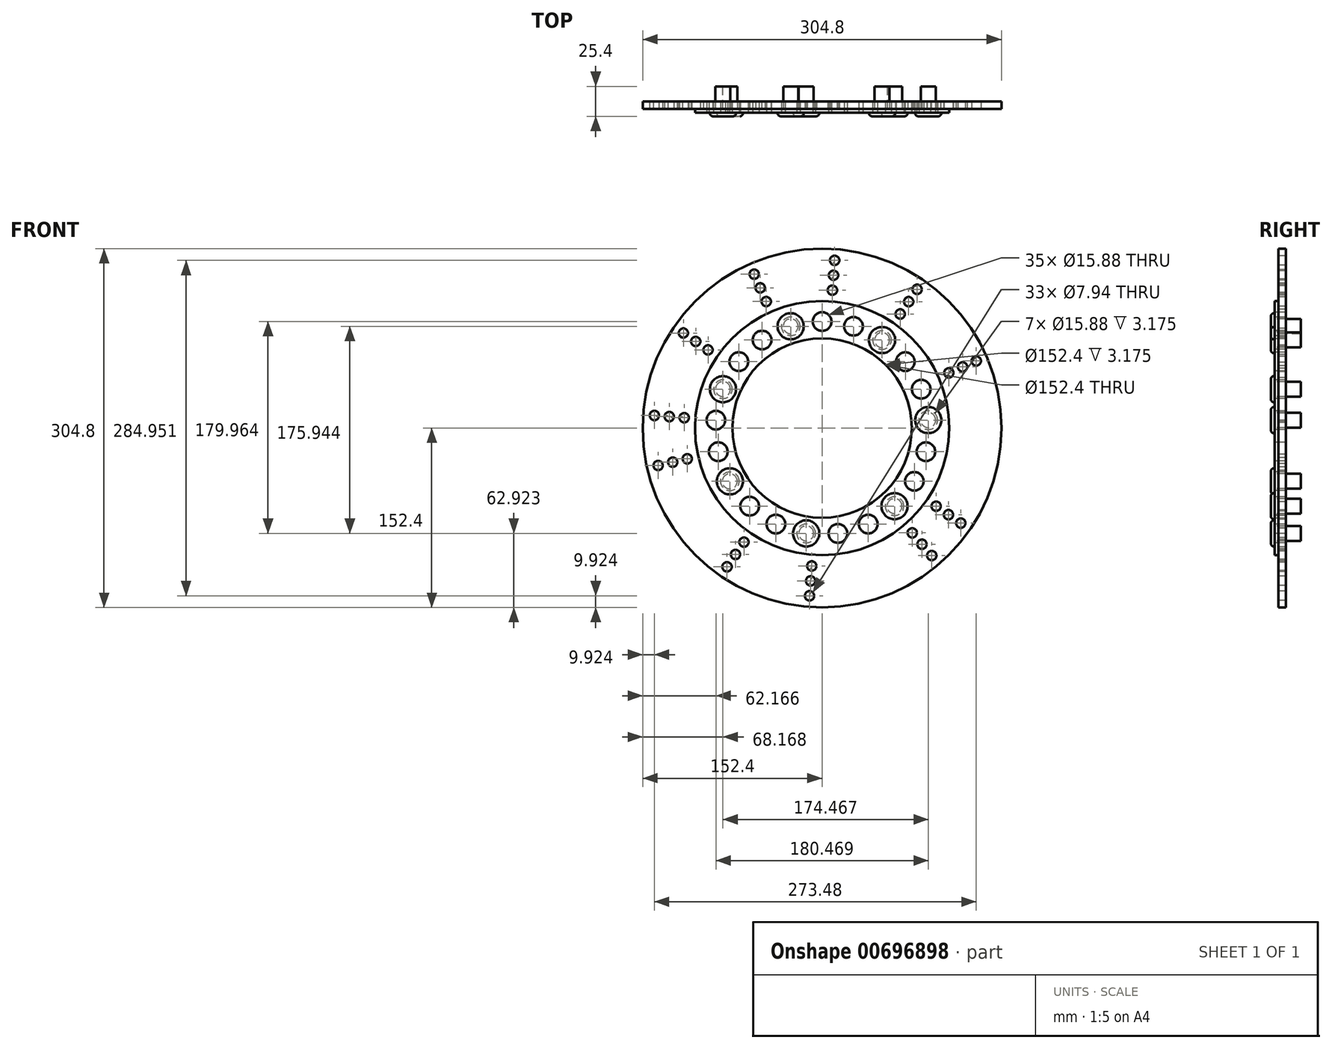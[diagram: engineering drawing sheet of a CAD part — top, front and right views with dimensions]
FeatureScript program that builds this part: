
annotation { "Feature Type Name" : "Feature", "Feature Type Description" : "" }
export const myFeature = defineFeature(function(context is Context, id is Id, definition is map)
    precondition{}
    {
        {
            var Q0;
            Q0=qCreatedBy(makeId("Front.planeOp"),FACE);
            var sketch = newSketch(context, id + "F0", { "sketchPlane" : qUnion([Q0])});
            skCircle(sketch, "E0", {"center": v(0, 0) * mm, "radius": 152.4 * mm});
            skCircle(sketch, "E1", {"center": v(0, 0) * mm, "radius": 76.2 * mm});
            skSolve(sketch);
        }
        {
            var Q0;
            Q0=qSketchRegion(id+"F0",true);
            extrude(context, id + "F1", {"entities" : qUnion([Q0]), "depth" : 6.35 * mm, "offsetDistance" : 25.4 * mm});
        }
        {
            var Q0;
            Q0=makeQuery(id+"F1.opExtrude","CAP_FACE",FACE,{"disambiguationData":[OSD([sQuery(id+"F0.wireOp",EDGE,"E0"),sQuery(id+"F0.wireOp",EDGE,"E1")])],"isStart":false});
            var sketch = newSketch(context, id + "F2", { "sketchPlane" : qUnion([Q0])});
            skCircle(sketch, "E2", {"center": v(0, 0) * mm, "radius": 76.2 * mm});
            skCircle(sketch, "E3", {"center": v(0, 0) * mm, "radius": 107.95 * mm});
            skSolve(sketch);
        }
        {
            var Q0;
            Q0=qSketchRegion(id+"F2",true);
            extrude(context, id + "F3", {"entities" : qUnion([Q0]), "depth" : 3.17 * mm, "offsetDistance" : 25.4 * mm});
        }
        {
            var Q0;
            Q0=makeQuery(id+"F3.opExtrude","CAP_FACE",FACE,{"disambiguationData":[OSD([sQuery(id+"F2.wireOp",EDGE,"E2"),sQuery(id+"F2.wireOp",EDGE,"E3")])],"isStart":false});
            var sketch = newSketch(context, id + "F4", { "sketchPlane" : qUnion([Q0])});
            skCircle(sketch, "E4", {"center": v(0, 90.49) * mm, "radius": 7.94 * mm});
            skCircle(sketch, "E5.1.0", {"center": v(-26.67, 86.47) * mm, "radius": 7.94 * mm});
            skCircle(sketch, "E5.2.0", {"center": v(-50.97, 74.76) * mm, "radius": 7.94 * mm});
            skCircle(sketch, "E5.3.0", {"center": v(-70.75, 56.42) * mm, "radius": 7.94 * mm});
            skCircle(sketch, "E5.4.0", {"center": v(-84.23, 33.06) * mm, "radius": 7.94 * mm});
            skCircle(sketch, "E5.5.0", {"center": v(-90.23, 6.76) * mm, "radius": 7.94 * mm});
            skCircle(sketch, "E5.6.0", {"center": v(-88.22, -20.14) * mm, "radius": 7.94 * mm});
            skCircle(sketch, "E5.7.0", {"center": v(-78.36, -45.24) * mm, "radius": 7.94 * mm});
            skCircle(sketch, "E5.8.0", {"center": v(-61.55, -66.33) * mm, "radius": 7.94 * mm});
            skCircle(sketch, "E5.9.0", {"center": v(-39.26, -81.53) * mm, "radius": 7.94 * mm});
            skCircle(sketch, "E5.10.0", {"center": v(-13.49, -89.48) * mm, "radius": 7.94 * mm});
            skCircle(sketch, "E5.11.0", {"center": v(13.49, -89.48) * mm, "radius": 7.94 * mm});
            skCircle(sketch, "E5.12.0", {"center": v(39.26, -81.53) * mm, "radius": 7.94 * mm});
            skCircle(sketch, "E5.13.0", {"center": v(61.55, -66.33) * mm, "radius": 7.94 * mm});
            skCircle(sketch, "E5.14.0", {"center": v(78.36, -45.24) * mm, "radius": 7.94 * mm});
            skCircle(sketch, "E5.15.0", {"center": v(88.22, -20.14) * mm, "radius": 7.94 * mm});
            skCircle(sketch, "E5.16.0", {"center": v(90.23, 6.76) * mm, "radius": 7.94 * mm});
            skCircle(sketch, "E5.17.0", {"center": v(84.23, 33.06) * mm, "radius": 7.94 * mm});
            skCircle(sketch, "E5.18.0", {"center": v(70.75, 56.42) * mm, "radius": 7.94 * mm});
            skCircle(sketch, "E5.19.0", {"center": v(50.97, 74.76) * mm, "radius": 7.94 * mm});
            skPoint(sketch, "E5.center", {"position": v(0, 0) * mm});
            skCircle(sketch, "E6.1.20.0", {"center": v(26.67, 86.47) * mm, "radius": 7.94 * mm});
            skSolve(sketch);
        }
        {
            var Q0;
            Q0=qSketchRegion(id+"F4",true);
            extrude(context, id + "F5", {"entities" : qUnion([Q0]), "operationType" : NewBodyOperationType.REMOVE, "endBound" : BoundingType.THROUGH_ALL, "oppositeDirection" : true, "depth" : 25.4 * mm, "offsetDistance" : 25.4 * mm});
        }
        {
            var Q0;
            Q0=makeQuery(id+"F3.opExtrude","CAP_FACE",FACE,{"disambiguationData":[OSD([sQuery(id+"F2.wireOp",EDGE,"E2"),sQuery(id+"F2.wireOp",EDGE,"E3")])],"isStart":false});
            var sketch = newSketch(context, id + "F6", { "sketchPlane" : qUnion([Q0])});
            skCircle(sketch, "E7", {"center": v(-13.49, -89.48) * mm, "radius": 11.11 * mm});
            skCircle(sketch, "E8", {"center": v(-78.36, -45.24) * mm, "radius": 11.11 * mm});
            skCircle(sketch, "E9", {"center": v(-84.23, 33.06) * mm, "radius": 11.11 * mm});
            skCircle(sketch, "E10", {"center": v(-26.67, 86.47) * mm, "radius": 11.11 * mm});
            skCircle(sketch, "E11", {"center": v(50.97, 74.76) * mm, "radius": 11.11 * mm});
            skCircle(sketch, "E12", {"center": v(90.23, 6.76) * mm, "radius": 11.11 * mm});
            skCircle(sketch, "E13", {"center": v(61.55, -66.33) * mm, "radius": 11.11 * mm});
            skSolve(sketch);
        }
        {
            var Q0;
            Q0=qSketchRegion(id+"F6",true);
            extrude(context, id + "F7", {"entities" : qUnion([Q0]), "operationType" : NewBodyOperationType.ADD, "depth" : 3.17 * mm, "offsetDistance" : 25.4 * mm});
        }
        {
            var Q0;
            Q0=makeQuery(id+"F1.opExtrude","CAP_FACE",FACE,{"disambiguationData":[OSD([sQuery(id+"F0.wireOp",EDGE,"E0"),sQuery(id+"F0.wireOp",EDGE,"E1")])],"isStart":false});
            var sketch = newSketch(context, id + "F8", { "sketchPlane" : qUnion([Q0])});
            skLineSegment(sketch, "E14", {"start": v(0, 107.95) * mm, "end": v(0, 152.4) * mm, "construction": true});
            skLineSegment(sketch, "E15", {"start": v(-7.94, 116.43) * mm, "end": v(7.94, 143.92) * mm, "construction": true});
            skCircle(sketch, "E16", {"center": v(0, 130.17) * mm, "radius": 3.97 * mm});
            skCircle(sketch, "E17", {"center": v(-7.94, 116.43) * mm, "radius": 3.97 * mm});
            skCircle(sketch, "E18", {"center": v(7.94, 143.92) * mm, "radius": 3.97 * mm});
            skCircle(sketch, "E19.1.0", {"center": v(-49.82, 120.27) * mm, "radius": 3.97 * mm});
            skCircle(sketch, "E19.1.1", {"center": v(-47.74, 136) * mm, "radius": 3.97 * mm});
            skCircle(sketch, "E19.1.2", {"center": v(-51.89, 104.53) * mm, "radius": 3.97 * mm});
            skCircle(sketch, "E19.2.0", {"center": v(-92.05, 92.05) * mm, "radius": 3.97 * mm});
            skCircle(sketch, "E19.2.1", {"center": v(-96.16, 107.38) * mm, "radius": 3.97 * mm});
            skCircle(sketch, "E19.2.2", {"center": v(-87.94, 76.71) * mm, "radius": 3.97 * mm});
            skCircle(sketch, "E19.3.0", {"center": v(-120.27, 49.82) * mm, "radius": 3.97 * mm});
            skCircle(sketch, "E19.3.1", {"center": v(-129.93, 62.41) * mm, "radius": 3.97 * mm});
            skCircle(sketch, "E19.3.2", {"center": v(-110.6, 37.22) * mm, "radius": 3.97 * mm});
            skCircle(sketch, "E19.4.0", {"center": v(-130.17, 0) * mm, "radius": 3.97 * mm});
            skCircle(sketch, "E19.4.1", {"center": v(-143.92, 7.94) * mm, "radius": 3.97 * mm});
            skCircle(sketch, "E19.4.2", {"center": v(-116.43, -7.94) * mm, "radius": 3.97 * mm});
            skCircle(sketch, "E19.5.0", {"center": v(-120.27, -49.82) * mm, "radius": 3.97 * mm});
            skCircle(sketch, "E19.5.1", {"center": v(-136, -47.74) * mm, "radius": 3.97 * mm});
            skCircle(sketch, "E19.5.2", {"center": v(-104.53, -51.89) * mm, "radius": 3.97 * mm});
            skCircle(sketch, "E19.6.0", {"center": v(-92.05, -92.05) * mm, "radius": 3.97 * mm});
            skCircle(sketch, "E19.6.1", {"center": v(-107.38, -96.16) * mm, "radius": 3.97 * mm});
            skCircle(sketch, "E19.6.2", {"center": v(-76.71, -87.94) * mm, "radius": 3.97 * mm});
            skCircle(sketch, "E19.7.0", {"center": v(-49.82, -120.27) * mm, "radius": 3.97 * mm});
            skCircle(sketch, "E19.7.1", {"center": v(-62.41, -129.93) * mm, "radius": 3.97 * mm});
            skCircle(sketch, "E19.7.2", {"center": v(-37.22, -110.6) * mm, "radius": 3.97 * mm});
            skCircle(sketch, "E19.8.0", {"center": v(0, -130.17) * mm, "radius": 3.97 * mm});
            skCircle(sketch, "E19.8.1", {"center": v(-7.94, -143.92) * mm, "radius": 3.97 * mm});
            skCircle(sketch, "E19.8.2", {"center": v(7.94, -116.43) * mm, "radius": 3.97 * mm});
            skCircle(sketch, "E19.9.0", {"center": v(49.82, -120.27) * mm, "radius": 3.97 * mm});
            skCircle(sketch, "E19.9.1", {"center": v(47.74, -136) * mm, "radius": 3.97 * mm});
            skCircle(sketch, "E19.9.2", {"center": v(51.89, -104.53) * mm, "radius": 3.97 * mm});
            skCircle(sketch, "E19.10.0", {"center": v(92.05, -92.05) * mm, "radius": 3.97 * mm});
            skCircle(sketch, "E19.10.1", {"center": v(96.16, -107.38) * mm, "radius": 3.97 * mm});
            skCircle(sketch, "E19.10.2", {"center": v(87.94, -76.71) * mm, "radius": 3.97 * mm});
            skCircle(sketch, "E19.11.0", {"center": v(120.27, -49.82) * mm, "radius": 3.97 * mm});
            skCircle(sketch, "E19.11.1", {"center": v(129.93, -62.41) * mm, "radius": 3.97 * mm});
            skCircle(sketch, "E19.11.2", {"center": v(110.6, -37.22) * mm, "radius": 3.97 * mm});
            skCircle(sketch, "E19.12.0", {"center": v(130.17, 0) * mm, "radius": 3.97 * mm});
            skCircle(sketch, "E19.12.1", {"center": v(143.92, -7.94) * mm, "radius": 3.97 * mm});
            skCircle(sketch, "E19.12.2", {"center": v(116.43, 7.94) * mm, "radius": 3.97 * mm});
            skCircle(sketch, "E19.13.0", {"center": v(120.27, 49.82) * mm, "radius": 3.97 * mm});
            skCircle(sketch, "E19.13.1", {"center": v(136, 47.74) * mm, "radius": 3.97 * mm});
            skCircle(sketch, "E19.13.2", {"center": v(104.53, 51.89) * mm, "radius": 3.97 * mm});
            skCircle(sketch, "E19.14.0", {"center": v(92.05, 92.05) * mm, "radius": 3.97 * mm});
            skCircle(sketch, "E19.14.1", {"center": v(107.38, 96.16) * mm, "radius": 3.97 * mm});
            skCircle(sketch, "E19.14.2", {"center": v(76.71, 87.94) * mm, "radius": 3.97 * mm});
            skCircle(sketch, "E19.15.0", {"center": v(49.82, 120.27) * mm, "radius": 3.97 * mm});
            skCircle(sketch, "E19.15.1", {"center": v(62.41, 129.93) * mm, "radius": 3.97 * mm});
            skCircle(sketch, "E19.15.2", {"center": v(37.22, 110.6) * mm, "radius": 3.97 * mm});
            skPoint(sketch, "E19.center", {"position": v(0, 0) * mm});
            skSolve(sketch);
        }
        {
            var Q0;
            Q0=makeQuery(id+"F7.opExtrude","CAP_FACE",FACE,{"disambiguationData":[OSD([sQuery(id+"F6.wireOp",EDGE,"E13")])],"isStart":false});
            var Q1;
            Q1=makeQuery(id+"F7.opExtrude","CAP_FACE",FACE,{"disambiguationData":[OSD([sQuery(id+"F6.wireOp",EDGE,"E7")])],"isStart":false});
            var Q2;
            Q2=makeQuery(id+"F7.opExtrude","CAP_FACE",FACE,{"disambiguationData":[OSD([sQuery(id+"F6.wireOp",EDGE,"E8")])],"isStart":false});
            var Q3;
            Q3=makeQuery(id+"F7.opExtrude","CAP_FACE",FACE,{"disambiguationData":[OSD([sQuery(id+"F6.wireOp",EDGE,"E9")])],"isStart":false});
            var Q4;
            Q4=makeQuery(id+"F7.opExtrude","CAP_FACE",FACE,{"disambiguationData":[OSD([sQuery(id+"F6.wireOp",EDGE,"E10")])],"isStart":false});
            var Q5;
            Q5=makeQuery(id+"F7.opExtrude","CAP_FACE",FACE,{"disambiguationData":[OSD([sQuery(id+"F6.wireOp",EDGE,"E11")])],"isStart":false});
            var Q6;
            Q6=makeQuery(id+"F7.opExtrude","CAP_FACE",FACE,{"disambiguationData":[OSD([sQuery(id+"F6.wireOp",EDGE,"E12")])],"isStart":false});
            fillet(context, id + "F9", {"entities" : qUnion([Q0, Q1, Q2, Q3, Q4, Q5, Q6]), "radius" : 2.54 * mm, "tangentPropagation" : true, "allowEdgeOverflow" : false});
        }
        {
            var Q0;
            Q0=makeQuery(id+"F7.opExtrude","CAP_FACE",FACE,{"disambiguationData":[OSD([sQuery(id+"F6.wireOp",EDGE,"E10")])],"isStart":false});
            var sketch = newSketch(context, id + "F10", { "sketchPlane" : qUnion([Q0])});
            skCircle(sketch, "E20", {"center": v(-26.67, 86.47) * mm, "radius": 6.35 * mm});
            skCircle(sketch, "E21.1.0", {"center": v(-84.23, 33.06) * mm, "radius": 6.35 * mm});
            skCircle(sketch, "E21.2.0", {"center": v(-78.36, -45.24) * mm, "radius": 6.35 * mm});
            skCircle(sketch, "E21.3.0", {"center": v(-13.49, -89.48) * mm, "radius": 6.35 * mm});
            skCircle(sketch, "E21.4.0", {"center": v(61.55, -66.33) * mm, "radius": 6.35 * mm});
            skCircle(sketch, "E21.5.0", {"center": v(90.23, 6.76) * mm, "radius": 6.35 * mm});
            skCircle(sketch, "E21.6.0", {"center": v(50.97, 74.76) * mm, "radius": 6.35 * mm});
            skPoint(sketch, "E21.center", {"position": v(0, 0) * mm});
            skSolve(sketch);
        }
        {
            var Q0;
            Q0=qSketchRegion(id+"F10",true);
            extrude(context, id + "F11", {"entities" : qUnion([Q0]), "operationType" : NewBodyOperationType.ADD, "oppositeDirection" : true, "depth" : 25.4 * mm, "offsetDistance" : 25.4 * mm});
        }
        {
            var Q0;
            Q0=makeQuery(id+"F8.imprint","IMPRINT",FACE,{"disambiguationData":[TD([[makeQuery(id+"F8.imprint","IMPRINT",EDGE,{"derivedFrom":sQuery(id+"F8.wireOp",EDGE,"E16")}),-1.0]])]});
            var sketch = newSketch(context, id + "F12", { "sketchPlane" : qUnion([Q0])});
            skLineSegment(sketch, "E22", {"start": v(0, 0) * mm, "end": v(-57.68, 130.72) * mm, "construction": true});
            skLineSegment(sketch, "E23", {"start": v(0, 0) * mm, "end": v(-117.86, 80.77) * mm, "construction": true});
            skLineSegment(sketch, "E24", {"start": v(0, 0) * mm, "end": v(-142.48, 10.68) * mm, "construction": true});
            skLineSegment(sketch, "E25", {"start": v(0, 0) * mm, "end": v(-139.3, -31.8) * mm, "construction": true});
            skLineSegment(sketch, "E26", {"start": v(0, 0) * mm, "end": v(-80.77, -117.86) * mm, "construction": true});
            skLineSegment(sketch, "E27", {"start": v(0, 0) * mm, "end": v(-10.68, -142.48) * mm, "construction": true});
            skLineSegment(sketch, "E28", {"start": v(0, 0) * mm, "end": v(93.17, -108.31) * mm, "construction": true});
            skLineSegment(sketch, "E29", {"start": v(0, 0) * mm, "end": v(117.86, -80.77) * mm, "construction": true});
            skLineSegment(sketch, "E30", {"start": v(0, 0) * mm, "end": v(131, 57.02) * mm, "construction": true});
            skLineSegment(sketch, "E31", {"start": v(0, 0) * mm, "end": v(80.77, 117.86) * mm, "construction": true});
            skLineSegment(sketch, "E32", {"start": v(0, 0) * mm, "end": v(10.68, 142.48) * mm, "construction": true});
            skCircle(sketch, "E33", {"center": v(0, 0) * mm, "radius": 142.88 * mm, "construction": true});
            skCircle(sketch, "E34", {"center": v(0, 0) * mm, "radius": 130.18 * mm, "construction": true});
            skCircle(sketch, "E35", {"center": v(0, 0) * mm, "radius": 117.48 * mm, "construction": true});
            skCircle(sketch, "E36", {"center": v(10.68, 142.48) * mm, "radius": 3.97 * mm});
            skCircle(sketch, "E37", {"center": v(9.73, 129.81) * mm, "radius": 3.97 * mm});
            skCircle(sketch, "E38", {"center": v(8.78, 117.15) * mm, "radius": 3.97 * mm});
            skCircle(sketch, "E39", {"center": v(-47.42, 107.48) * mm, "radius": 3.97 * mm});
            skCircle(sketch, "E40", {"center": v(-52.55, 119.1) * mm, "radius": 3.97 * mm});
            skCircle(sketch, "E41", {"center": v(-57.68, 130.72) * mm, "radius": 3.97 * mm});
            skCircle(sketch, "E42", {"center": v(-96.9, 66.4) * mm, "radius": 3.97 * mm});
            skCircle(sketch, "E43", {"center": v(-107.38, 73.59) * mm, "radius": 3.97 * mm});
            skCircle(sketch, "E44", {"center": v(-117.86, 80.77) * mm, "radius": 3.97 * mm});
            skCircle(sketch, "E45", {"center": v(-142.48, 10.68) * mm, "radius": 3.97 * mm});
            skCircle(sketch, "E46", {"center": v(-129.81, 9.73) * mm, "radius": 3.97 * mm});
            skCircle(sketch, "E47", {"center": v(-117.15, 8.78) * mm, "radius": 3.97 * mm});
            skCircle(sketch, "E48", {"center": v(-139.3, -31.8) * mm, "radius": 3.97 * mm});
            skCircle(sketch, "E49", {"center": v(-126.91, -28.97) * mm, "radius": 3.97 * mm});
            skCircle(sketch, "E50", {"center": v(-114.53, -26.14) * mm, "radius": 3.97 * mm});
            skCircle(sketch, "E51", {"center": v(-80.77, -117.86) * mm, "radius": 3.97 * mm});
            skCircle(sketch, "E52", {"center": v(-73.59, -107.38) * mm, "radius": 3.97 * mm});
            skCircle(sketch, "E53", {"center": v(-66.4, -96.9) * mm, "radius": 3.97 * mm});
            skCircle(sketch, "E54", {"center": v(-10.68, -142.48) * mm, "radius": 3.97 * mm});
            skCircle(sketch, "E55", {"center": v(-9.73, -129.81) * mm, "radius": 3.97 * mm});
            skCircle(sketch, "E56", {"center": v(-8.78, -117.15) * mm, "radius": 3.97 * mm});
            skCircle(sketch, "E57", {"center": v(93.17, -108.31) * mm, "radius": 3.97 * mm});
            skCircle(sketch, "E58", {"center": v(84.9, -98.69) * mm, "radius": 3.97 * mm});
            skCircle(sketch, "E59", {"center": v(76.6, -89.06) * mm, "radius": 3.97 * mm});
            skCircle(sketch, "E60", {"center": v(117.86, -80.77) * mm, "radius": 3.97 * mm});
            skCircle(sketch, "E61", {"center": v(107.38, -73.59) * mm, "radius": 3.97 * mm});
            skCircle(sketch, "E62", {"center": v(96.9, -66.4) * mm, "radius": 3.97 * mm});
            skCircle(sketch, "E63", {"center": v(107.71, 46.88) * mm, "radius": 3.97 * mm});
            skCircle(sketch, "E64", {"center": v(119.36, 51.95) * mm, "radius": 3.97 * mm});
            skCircle(sketch, "E65", {"center": v(131, 57.02) * mm, "radius": 3.97 * mm});
            skCircle(sketch, "E66", {"center": v(66.4, 96.9) * mm, "radius": 3.97 * mm});
            skCircle(sketch, "E67", {"center": v(73.59, 107.38) * mm, "radius": 3.97 * mm});
            skCircle(sketch, "E68", {"center": v(80.77, 117.86) * mm, "radius": 3.97 * mm});
            skSolve(sketch);
        }
        {
            var Q0;
            Q0=qSketchRegion(id+"F12",true);
            extrude(context, id + "F13", {"entities" : qUnion([Q0]), "operationType" : NewBodyOperationType.REMOVE, "endBound" : BoundingType.UP_TO_NEXT, "oppositeDirection" : true, "depth" : 25.4 * mm, "offsetDistance" : 25.4 * mm});
        }
    });
